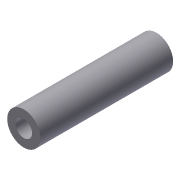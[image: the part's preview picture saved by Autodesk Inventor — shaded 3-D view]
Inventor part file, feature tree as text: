
AUTODESK INVENTOR PART (.ipt)
format: ipt  version: 2011 SP1 (Build 150282100, 282)  size: 71,168 bytes
history: native  units: in
note: dims shown in document units (in); Inventor stores cm internally (conversion verified against a paired STEP export)
features: extrude x1, sketch x1
ambient origin geometry x8: Origin, YZ Plane, XZ Plane, XY Plane, X Axis, Y Axis, Z Axis, Center Point
bodies: Solid1 (feature_tree)
feature tree (2):
  extrude  "Extrusion1"  Depth=0.25in
  sketch  "Sketch1"  dims[d0=0.5in d1=0.25in d2=2.0in d3=0.0in]
